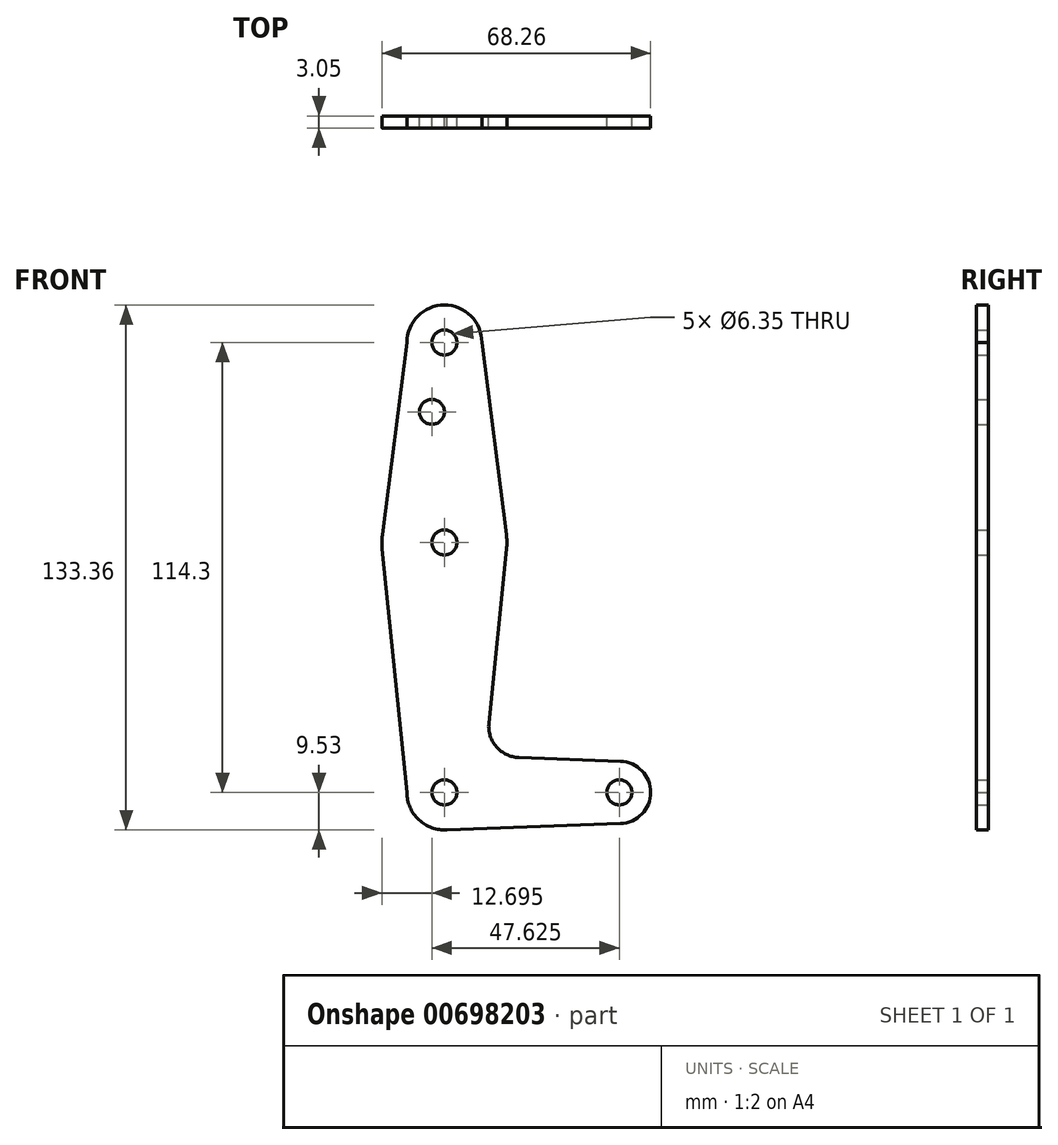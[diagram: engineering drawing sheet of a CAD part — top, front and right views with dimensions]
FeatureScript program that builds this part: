
annotation { "Feature Type Name" : "Feature", "Feature Type Description" : "" }
export const myFeature = defineFeature(function(context is Context, id is Id, definition is map)
    precondition{}
    {
        {
            var Q0;
            Q0=qCreatedBy(makeId("Front.planeOp"),FACE);
            var sketch = newSketch(context, id + "F0", { "sketchPlane" : qUnion([Q0])});
            skLineSegment(sketch, "E0", {"start": v(0, 0) * mm, "end": v(0, 114.3) * mm});
            skLineSegment(sketch, "E1", {"start": v(0, 0) * mm, "end": v(44.45, 0) * mm});
            skCircle(sketch, "E2", {"center": v(0, 114.3) * mm, "radius": 9.53 * mm});
            skCircle(sketch, "E3", {"center": v(0, 0) * mm, "radius": 9.53 * mm});
            skCircle(sketch, "E4", {"center": v(44.45, 0) * mm, "radius": 7.94 * mm});
            skLineSegment(sketch, "E5", {"start": v(0, -9.53) * mm, "end": v(44.73, -7.93) * mm});
            skLineSegment(sketch, "E6", {"start": v(18.93, 8.85) * mm, "end": v(44.73, 7.93) * mm});
            skCircle(sketch, "E7", {"center": v(0, 63.5) * mm, "radius": 15.88 * mm});
            skLineSegment(sketch, "E8", {"start": v(-9.53, 114.3) * mm, "end": v(-15.75, 65.5) * mm});
            skLineSegment(sketch, "E9", {"start": v(9.53, 114.3) * mm, "end": v(15.75, 65.5) * mm});
            skLineSegment(sketch, "E10", {"start": v(-9.53, 0) * mm, "end": v(-15.8, 61.9) * mm});
            skLineSegment(sketch, "E11", {"start": v(11.3, 17.6) * mm, "end": v(15.8, 61.9) * mm});
            skCircle(sketch, "E12", {"center": v(0, 114.3) * mm, "radius": 3.18 * mm});
            skCircle(sketch, "E13", {"center": v(0, 63.5) * mm, "radius": 3.18 * mm});
            skCircle(sketch, "E14", {"center": v(0, 0) * mm, "radius": 3.18 * mm});
            skCircle(sketch, "E15", {"center": v(44.45, 0) * mm, "radius": 3.18 * mm});
            skCircle(sketch, "E16", {"center": v(-3.18, 96.7) * mm, "radius": 3.18 * mm});
            skArc(sketch, "E17.filletArc", {"start": v(11.3, 17.6) * mm, "mid": v(13.22, 11.57) * mm, "end": v(18.93, 8.85) * mm});
            skSolve(sketch);
        }
        {
            var Q0;
            Q0 = qSketchRegion(id + "F0", true);
            var Q1;
            {var subQ0=sQuery(id+"F0.wireOp",EDGE,"E14");var subQ1=sQuery(id+"F0.wireOp",EDGE,"E0");var subQ2=makeQuery(id+"F0.imprint","INTERSECT",VERTEX,{"derivedFrom":[subQ1,subQ0]});Q1=makeQuery(id+"F0.imprint","IMPRINT",FACE,{"disambiguationData":[TD([[makeQuery(id+"F0.imprint","IMPRINT",EDGE,{"disambiguationData":[TD([[subQ2,-1.0]])],"derivedFrom":subQ1}),-1.0]])]});}
            extrude(context, id + "F1", {"entities" : qUnion([Q0, Q1]), "depth" : 3.05 * mm, "offsetDistance" : 25.4 * mm});
        }
    });
